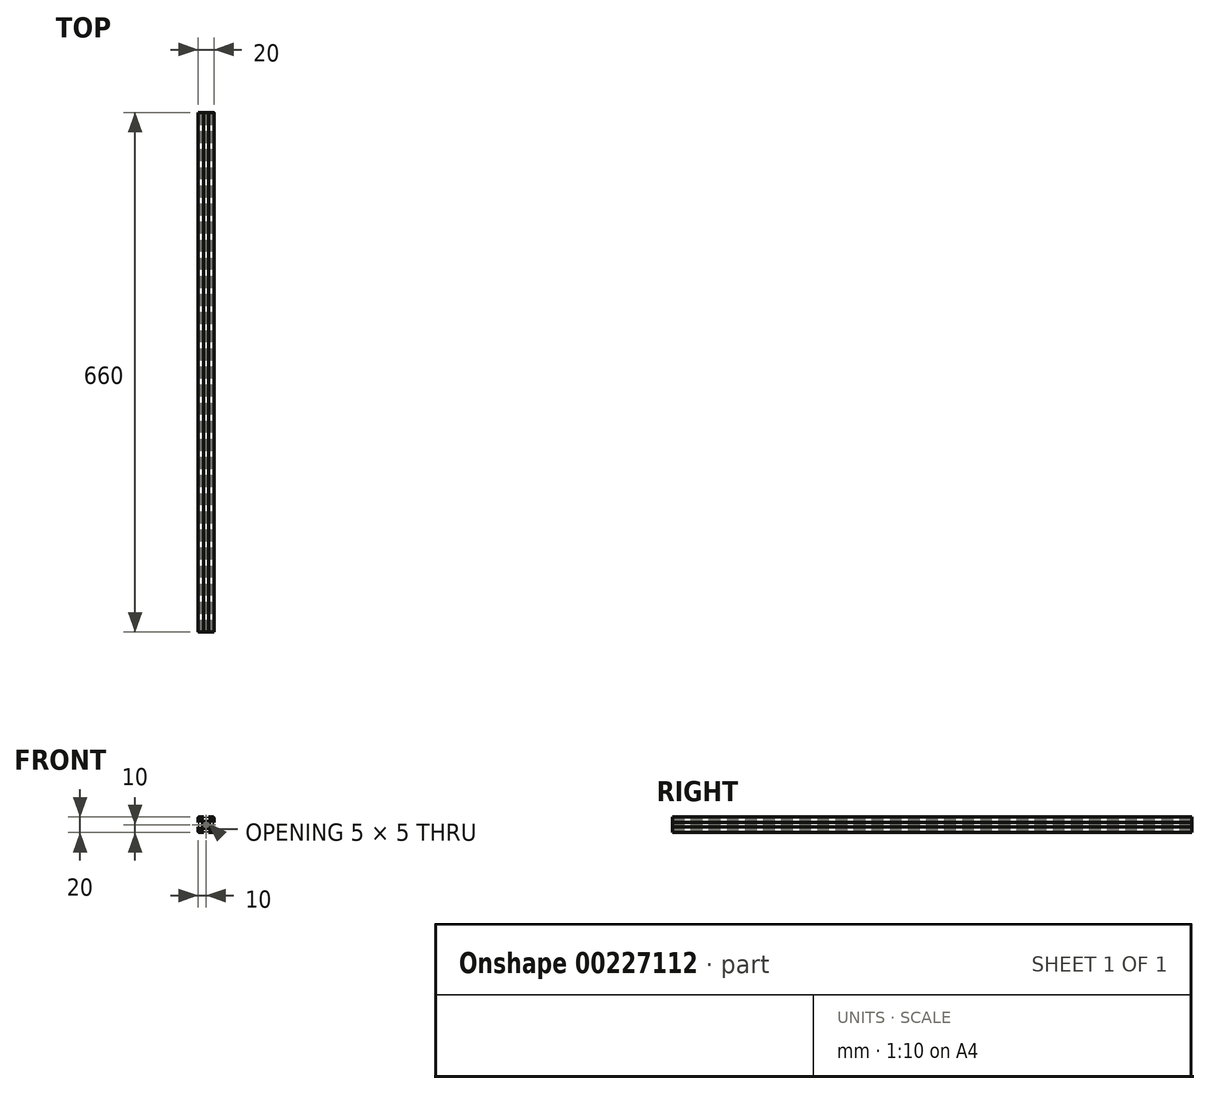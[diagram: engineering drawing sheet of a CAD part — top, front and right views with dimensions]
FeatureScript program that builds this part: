
annotation { "Feature Type Name" : "Feature", "Feature Type Description" : "" }
export const myFeature = defineFeature(function(context is Context, id is Id, definition is map)
    precondition{}
    {
        {
            var Q0;
            Q0=qCreatedBy(makeId("Front.planeOp"),FACE);
            var sketch = newSketch(context, id + "F0", { "sketchPlane" : qUnion([Q0])});
            skLineSegment(sketch, "E0.bottom", {"start": v(8.5, -10) * mm, "end": v(3, -10) * mm});
            skLineSegment(sketch, "E0.top", {"start": v(8.5, 10) * mm, "end": v(3, 10) * mm});
            skLineSegment(sketch, "E0.left", {"start": v(10, -8.5) * mm, "end": v(10, -3) * mm});
            skLineSegment(sketch, "E0.right", {"start": v(-10, -8.5) * mm, "end": v(-10, -3) * mm});
            skPoint(sketch, "E0.middle", {"position": v(0, 0) * mm});
            skLineSegment(sketch, "E1.bottom", {"start": v(6, -8.5) * mm, "end": v(3, -8.5) * mm});
            skLineSegment(sketch, "E1.top", {"start": v(6, 8.5) * mm, "end": v(3, 8.5) * mm});
            skLineSegment(sketch, "E1.left", {"start": v(8.5, -6) * mm, "end": v(8.5, -3) * mm});
            skLineSegment(sketch, "E1.right", {"start": v(-8.5, -6) * mm, "end": v(-8.5, -3) * mm});
            skLineSegment(sketch, "E2.bottom", {"start": v(3.44, -4.5) * mm, "end": v(-3.44, -4.5) * mm});
            skLineSegment(sketch, "E2.top", {"start": v(3.44, 4.5) * mm, "end": v(-3.44, 4.5) * mm});
            skLineSegment(sketch, "E2.left", {"start": v(4.5, -3.44) * mm, "end": v(4.5, 3.44) * mm});
            skLineSegment(sketch, "E2.right", {"start": v(-4.5, -3.44) * mm, "end": v(-4.5, 3.44) * mm});
            skLineSegment(sketch, "E3.bottom", {"start": v(8.5, -6) * mm, "end": v(7.06, -6) * mm});
            skLineSegment(sketch, "E3.top", {"start": v(8.5, 6) * mm, "end": v(7.06, 6) * mm});
            skLineSegment(sketch, "E4.left", {"start": v(6, -8.5) * mm, "end": v(6, -7.06) * mm});
            skLineSegment(sketch, "E4.right", {"start": v(-6, -8.5) * mm, "end": v(-6, -7.06) * mm});
            skPoint(sketch, "E5.orphan", {"position": v(-8.5, 8.5) * mm});
            skPoint(sketch, "E6.orphan", {"position": v(8.5, 8.5) * mm});
            skPoint(sketch, "E7.orphan", {"position": v(8.5, -8.5) * mm});
            skPoint(sketch, "E8.orphan", {"position": v(-8.5, -8.5) * mm});
            skLineSegment(sketch, "E9.trimOffspring", {"start": v(-6, 7.06) * mm, "end": v(-6, 8.5) * mm});
            skLineSegment(sketch, "E10.trimOffspring", {"start": v(-7.06, 6) * mm, "end": v(-8.5, 6) * mm});
            skLineSegment(sketch, "E11.trimOffspring", {"start": v(6, 7.06) * mm, "end": v(6, 8.5) * mm});
            skLineSegment(sketch, "E12.trimOffspring", {"start": v(-7.06, -6) * mm, "end": v(-8.5, -6) * mm});
            skLineSegment(sketch, "E13", {"start": v(-10, 10) * mm, "end": v(0, 0) * mm, "construction": true});
            skLineSegment(sketch, "E14", {"start": v(10, 10) * mm, "end": v(0, 0) * mm, "construction": true});
            skLineSegment(sketch, "E15", {"start": v(-6, 7.06) * mm, "end": v(-3.44, 4.5) * mm});
            skPoint(sketch, "E15.endSnap0", {"position": v(7.25, -6) * mm});
            skLineSegment(sketch, "E16", {"start": v(6, -7.06) * mm, "end": v(3.44, -4.5) * mm});
            skLineSegment(sketch, "E17", {"start": v(7.06, 6) * mm, "end": v(4.5, 3.44) * mm});
            skLineSegment(sketch, "E18", {"start": v(6, 7.06) * mm, "end": v(3.44, 4.5) * mm});
            skPoint(sketch, "E19.orphan", {"position": v(6, -6) * mm});
            skPoint(sketch, "E20.orphan", {"position": v(-4.5, -4.5) * mm});
            skPoint(sketch, "E21.orphan", {"position": v(-4.5, 4.5) * mm});
            skPoint(sketch, "E22.orphan", {"position": v(4.5, 4.5) * mm});
            skPoint(sketch, "E23.orphan", {"position": v(4.5, -4.5) * mm});
            skLineSegment(sketch, "E24.trimOffspring", {"start": v(4.5, -3.44) * mm, "end": v(7.06, -6) * mm});
            skLineSegment(sketch, "E25.trimOffspring", {"start": v(-3.44, -4.5) * mm, "end": v(-6, -7.06) * mm});
            skLineSegment(sketch, "E26.trimOffspring", {"start": v(-4.5, -3.44) * mm, "end": v(-7.06, -6) * mm});
            skLineSegment(sketch, "E27.trimOffspring", {"start": v(-4.5, 3.44) * mm, "end": v(-7.06, 6) * mm});
            skLineSegment(sketch, "E28.bottom", {"start": v(8.5, -3) * mm, "end": v(10, -3) * mm});
            skLineSegment(sketch, "E28.top", {"start": v(8.5, 3) * mm, "end": v(10, 3) * mm});
            skPoint(sketch, "E28.middle", {"position": v(10, 0) * mm});
            skLineSegment(sketch, "E29.left", {"start": v(3, 8.5) * mm, "end": v(3, 10) * mm});
            skLineSegment(sketch, "E29.right", {"start": v(-3, 8.5) * mm, "end": v(-3, 10) * mm});
            skPoint(sketch, "E29.middle", {"position": v(0, 10) * mm});
            skLineSegment(sketch, "E30.bottom", {"start": v(-8.5, 3) * mm, "end": v(-10, 3) * mm});
            skLineSegment(sketch, "E30.top", {"start": v(-8.5, -3) * mm, "end": v(-10, -3) * mm});
            skPoint(sketch, "E30.middle", {"position": v(-10, 0) * mm});
            skLineSegment(sketch, "E31.left", {"start": v(3, -8.5) * mm, "end": v(3, -10) * mm});
            skLineSegment(sketch, "E31.right", {"start": v(-3, -8.5) * mm, "end": v(-3, -10) * mm});
            skPoint(sketch, "E31.middle", {"position": v(0, -10) * mm});
            skPoint(sketch, "E32.orphan", {"position": v(3, 11.5) * mm});
            skPoint(sketch, "E33.orphan", {"position": v(-3, 11.5) * mm});
            skLineSegment(sketch, "E34.trimOffspring", {"start": v(-3, 10) * mm, "end": v(-8.5, 10) * mm});
            skLineSegment(sketch, "E35.trimOffspring", {"start": v(-3, 8.5) * mm, "end": v(-6, 8.5) * mm});
            skPoint(sketch, "E28.right.end.orphan", {"position": v(11.5, 3) * mm});
            skPoint(sketch, "E36.orphan", {"position": v(11.5, -3) * mm});
            skLineSegment(sketch, "E37.trimOffspring", {"start": v(10, 3) * mm, "end": v(10, 8.5) * mm});
            skLineSegment(sketch, "E38.trimOffspring", {"start": v(8.5, 3) * mm, "end": v(8.5, 6) * mm});
            skPoint(sketch, "E39.orphan", {"position": v(3, -11.5) * mm});
            skPoint(sketch, "E40.orphan", {"position": v(-3, -11.5) * mm});
            skLineSegment(sketch, "E41.trimOffspring", {"start": v(-3, -10) * mm, "end": v(-8.5, -10) * mm});
            skLineSegment(sketch, "E42.trimOffspring", {"start": v(-3, -8.5) * mm, "end": v(-6, -8.5) * mm});
            skPoint(sketch, "E30.right.end.orphan", {"position": v(-11.5, -3) * mm});
            skPoint(sketch, "E43.orphan", {"position": v(-11.5, 3) * mm});
            skLineSegment(sketch, "E44.trimOffspring", {"start": v(-10, 3) * mm, "end": v(-10, 8.5) * mm});
            skLineSegment(sketch, "E45.trimOffspring", {"start": v(-8.5, 3) * mm, "end": v(-8.5, 6) * mm});
            skLineSegment(sketch, "E46.trimOffspring", {"start": v(0, 0) * mm, "end": v(10, -10) * mm, "construction": true});
            skLineSegment(sketch, "E47.trimOffspring", {"start": v(0, 0) * mm, "end": v(-10, -10) * mm, "construction": true});
            skArc(sketch, "E48", {"start": v(1.16, 2.22) * mm, "mid": v(0, 2.5) * mm, "end": v(-1.16, 2.22) * mm});
            skLineSegment(sketch, "E49", {"start": v(-2.5, -1.44) * mm, "end": v(1.44, 2.5) * mm});
            skLineSegment(sketch, "E50", {"start": v(2.5, 1.44) * mm, "end": v(-1.44, -2.5) * mm});
            skLineSegment(sketch, "E51", {"start": v(1.44, -2.5) * mm, "end": v(-2.5, 1.44) * mm});
            skLineSegment(sketch, "E52", {"start": v(-1.44, 2.5) * mm, "end": v(2.5, -1.44) * mm});
            skLineSegment(sketch, "E53", {"start": v(2.5, 1.44) * mm, "end": v(2.5, -1.44) * mm, "construction": true});
            skLineSegment(sketch, "E54", {"start": v(1.44, -2.5) * mm, "end": v(-1.44, -2.5) * mm, "construction": true});
            skLineSegment(sketch, "E55", {"start": v(-2.5, -1.44) * mm, "end": v(-2.5, 1.44) * mm, "construction": true});
            skLineSegment(sketch, "E56", {"start": v(-1.44, 2.5) * mm, "end": v(1.44, 2.5) * mm, "construction": true});
            skLineSegment(sketch, "E57", {"start": v(-1.44, 2.5) * mm, "end": v(-2.5, 1.44) * mm});
            skLineSegment(sketch, "E58", {"start": v(1.44, 2.5) * mm, "end": v(2.5, 1.44) * mm});
            skLineSegment(sketch, "E59", {"start": v(2.5, -1.44) * mm, "end": v(1.44, -2.5) * mm});
            skLineSegment(sketch, "E60", {"start": v(-1.44, -2.5) * mm, "end": v(-2.5, -1.44) * mm});
            skArc(sketch, "E61.trimOffspring", {"start": v(-2.22, 1.16) * mm, "mid": v(-2.5, 0) * mm, "end": v(-2.22, -1.16) * mm});
            skArc(sketch, "E62.trimOffspring", {"start": v(-1.16, -2.22) * mm, "mid": v(0, -2.5) * mm, "end": v(1.16, -2.22) * mm});
            skArc(sketch, "E63.trimOffspring", {"start": v(2.22, -1.16) * mm, "mid": v(2.5, 0) * mm, "end": v(2.22, 1.16) * mm});
            skPoint(sketch, "E64.visualSharp", {"position": v(10, 10) * mm});
            skArc(sketch, "E64.filletArc", {"start": v(10, 8.5) * mm, "mid": v(9.56, 9.56) * mm, "end": v(8.5, 10) * mm});
            skPoint(sketch, "E65.visualSharp", {"position": v(10, -10) * mm});
            skArc(sketch, "E65.filletArc", {"start": v(8.5, -10) * mm, "mid": v(9.56, -9.56) * mm, "end": v(10, -8.5) * mm});
            skPoint(sketch, "E66.visualSharp", {"position": v(-10, -10) * mm});
            skArc(sketch, "E66.filletArc", {"start": v(-10, -8.5) * mm, "mid": v(-9.56, -9.56) * mm, "end": v(-8.5, -10) * mm});
            skPoint(sketch, "E67.visualSharp", {"position": v(-10, 10) * mm});
            skArc(sketch, "E67.filletArc", {"start": v(-8.5, 10) * mm, "mid": v(-9.56, 9.56) * mm, "end": v(-10, 8.5) * mm});
            skSolve(sketch);
        }
        {
            assignVariable(context, id + "F2", {"name" : "Length", "anyValue" : 660});
        }
        {
            var Q0;
            Q0=qSketchRegion(id+"F0",true);
            extrude(context, id + "F1", {"entities" : qUnion([Q0]), "depth" : (getVariable(context, 'Length')) * mm});
        }
    });
